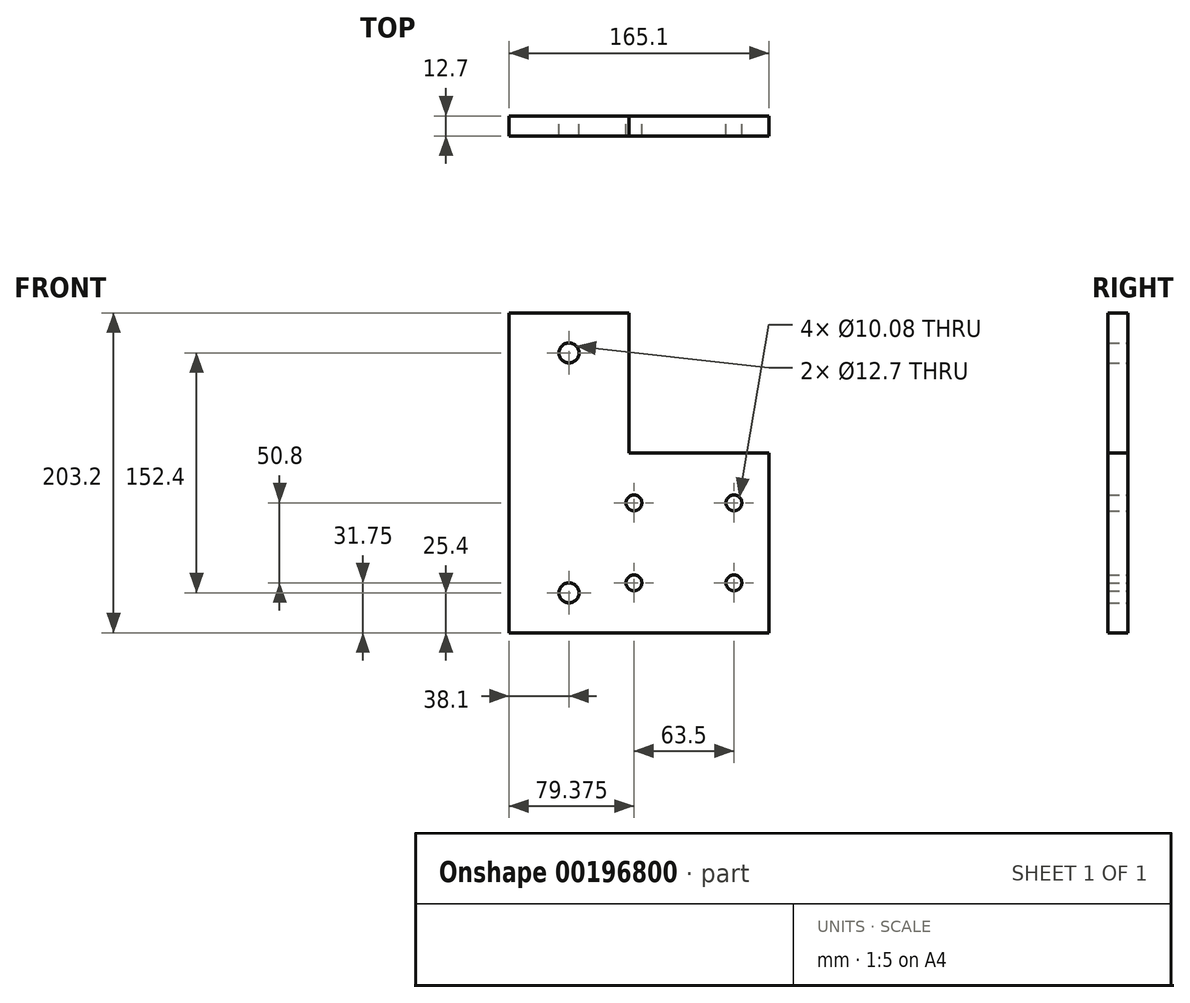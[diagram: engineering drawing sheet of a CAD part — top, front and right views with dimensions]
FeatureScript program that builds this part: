
annotation { "Feature Type Name" : "Feature", "Feature Type Description" : "" }
export const myFeature = defineFeature(function(context is Context, id is Id, definition is map)
    precondition{}
    {
        {
            var Q0;
            Q0=qCreatedBy(makeId("Front.planeOp"),FACE);
            var sketch = newSketch(context, id + "F0", { "sketchPlane" : qUnion([Q0])});
            skLineSegment(sketch, "E0.bottom", {"start": v(-6.35, 101.6) * mm, "end": v(-82.55, 101.6) * mm});
            skLineSegment(sketch, "E0.top", {"start": v(82.55, -101.6) * mm, "end": v(-82.55, -101.6) * mm});
            skLineSegment(sketch, "E0.left", {"start": v(82.55, 12.7) * mm, "end": v(82.55, -101.6) * mm});
            skLineSegment(sketch, "E0.right", {"start": v(-82.55, 101.6) * mm, "end": v(-82.55, -101.6) * mm});
            skPoint(sketch, "E0.middle", {"position": v(0, 0) * mm});
            skLineSegment(sketch, "E1", {"start": v(-6.35, 101.6) * mm, "end": v(-6.35, 12.7) * mm});
            skPoint(sketch, "E1.endSnap0", {"position": v(-6.35, 101.6) * mm});
            skLineSegment(sketch, "E2", {"start": v(-6.35, 12.7) * mm, "end": v(82.55, 12.7) * mm});
            skCircle(sketch, "E3", {"center": v(-44.45, 76.2) * mm, "radius": 6.35 * mm});
            skPoint(sketch, "E3.centerSnap0", {"position": v(-44.45, 101.6) * mm});
            skCircle(sketch, "E4.MirrorC", {"center": v(-44.45, -76.2) * mm, "radius": 6.35 * mm});
            skCircle(sketch, "E5", {"center": v(60.33, -19.05) * mm, "radius": 5.04 * mm});
            skCircle(sketch, "E6", {"center": v(-3.17, -19.05) * mm, "radius": 5.04 * mm});
            skCircle(sketch, "E7", {"center": v(-3.17, -69.85) * mm, "radius": 5.04 * mm});
            skCircle(sketch, "E8", {"center": v(60.33, -69.85) * mm, "radius": 5.04 * mm});
            skSolve(sketch);
        }
        {
            var Q0;
            Q0=makeQuery(id+"F0.imprint","IMPRINT",FACE,{"disambiguationData":[TD([[makeQuery(id+"F0.imprint","IMPRINT",EDGE,{"derivedFrom":sQuery(id+"F0.wireOp",EDGE,"E0.bottom")}),1.0]])]});
            extrude(context, id + "F1", {"entities" : qUnion([Q0]), "endBound" : BoundingType.SYMMETRIC, "depth" : 12.7 * mm});
        }
    });
